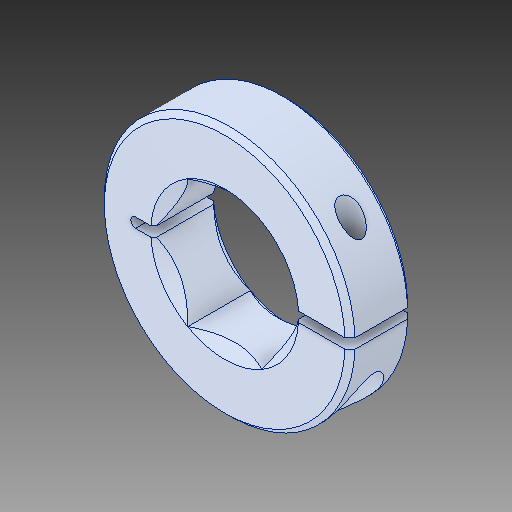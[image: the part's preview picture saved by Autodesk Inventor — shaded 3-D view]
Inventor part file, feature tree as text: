
AUTODESK INVENTOR PART (.ipt)
format: ipt  version: 2017 (Build 210142000, 142)  size: 164,864 bytes
history: native  units: in
note: dims shown in document units (in); Inventor stores cm internally (conversion verified against a paired STEP export)
features: chamfer x1
ambient origin geometry x8: Origin, YZ Plane, XZ Plane, XY Plane, X Axis, Y Axis, Z Axis, Center Point
bodies: Solid1 (feature_tree)
feature tree (1):
  chamfer  "Chamfer2"  [1 undecoded]
note: 1 required parameter value undecoded (feature->parameter linkage not recoverable at this tier; creation-order binding heuristic only, values carry confidence <= 0.55)
